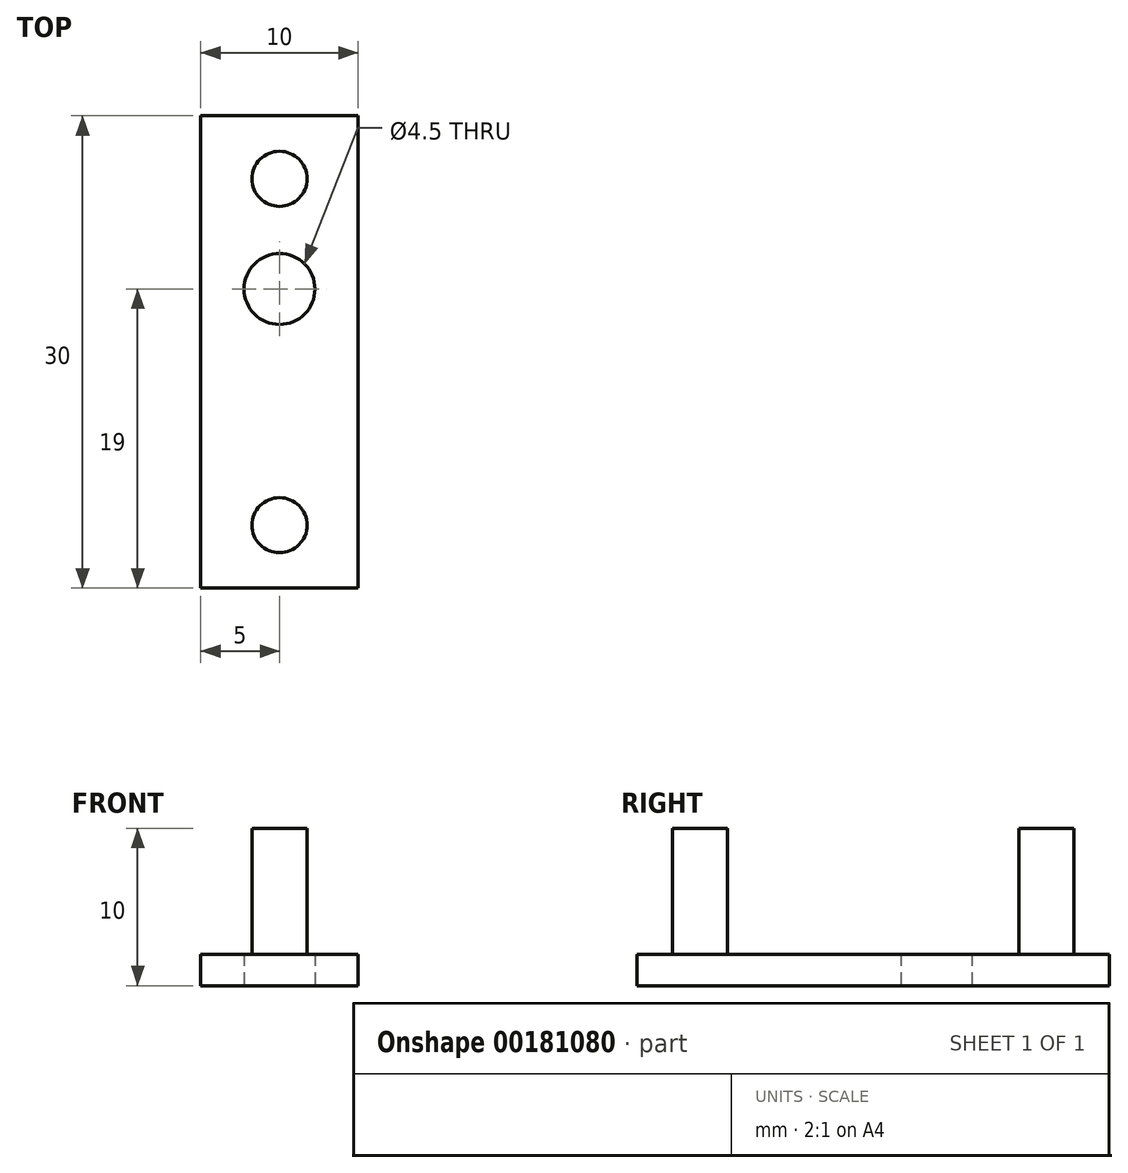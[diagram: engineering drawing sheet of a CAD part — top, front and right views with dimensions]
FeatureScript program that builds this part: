
annotation { "Feature Type Name" : "Feature", "Feature Type Description" : "" }
export const myFeature = defineFeature(function(context is Context, id is Id, definition is map)
    precondition{}
    {
        {
            var Q0;
            Q0=qCreatedBy(makeId("Top.planeOp"),FACE);
            var sketch = newSketch(context, id + "F0", { "sketchPlane" : qUnion([Q0])});
            skLineSegment(sketch, "E0.bottom", {"start": v(5, -15) * mm, "end": v(-5, -15) * mm});
            skLineSegment(sketch, "E0.top", {"start": v(5, 15) * mm, "end": v(-5, 15) * mm});
            skLineSegment(sketch, "E0.left", {"start": v(5, -15) * mm, "end": v(5, 15) * mm});
            skLineSegment(sketch, "E0.right", {"start": v(-5, -15) * mm, "end": v(-5, 15) * mm});
            skPoint(sketch, "E0.middle", {"position": v(0, 0) * mm});
            skCircle(sketch, "E1", {"center": v(0, 11) * mm, "radius": 1.75 * mm});
            skCircle(sketch, "E2", {"center": v(0, -11) * mm, "radius": 1.75 * mm});
            skCircle(sketch, "E3", {"center": v(0, 4) * mm, "radius": 2.25 * mm});
            skSolve(sketch);
        }
        {
            var Q0;
            Q0=makeQuery(id+"F0.imprint","IMPRINT",FACE,{"disambiguationData":[TD([[makeQuery(id+"F0.imprint","IMPRINT",EDGE,{"derivedFrom":sQuery(id+"F0.wireOp",EDGE,"E1")}),1.0]])]});
            var Q1;
            Q1=makeQuery(id+"F0.imprint","IMPRINT",FACE,{"disambiguationData":[TD([[makeQuery(id+"F0.imprint","IMPRINT",EDGE,{"derivedFrom":sQuery(id+"F0.wireOp",EDGE,"E2")}),1.0]])]});
            extrude(context, id + "F1", {"entities" : qUnion([Q0, Q1]), "depth" : 10 * mm});
        }
        {
            var Q0;
            Q0=makeQuery(id+"F0.imprint","IMPRINT",FACE,{"disambiguationData":[TD([[makeQuery(id+"F0.imprint","IMPRINT",EDGE,{"derivedFrom":sQuery(id+"F0.wireOp",EDGE,"E0.bottom")}),-1.0]])]});
            extrude(context, id + "F2", {"entities" : qUnion([Q0]), "operationType" : NewBodyOperationType.ADD, "depth" : 2 * mm});
        }
    });
